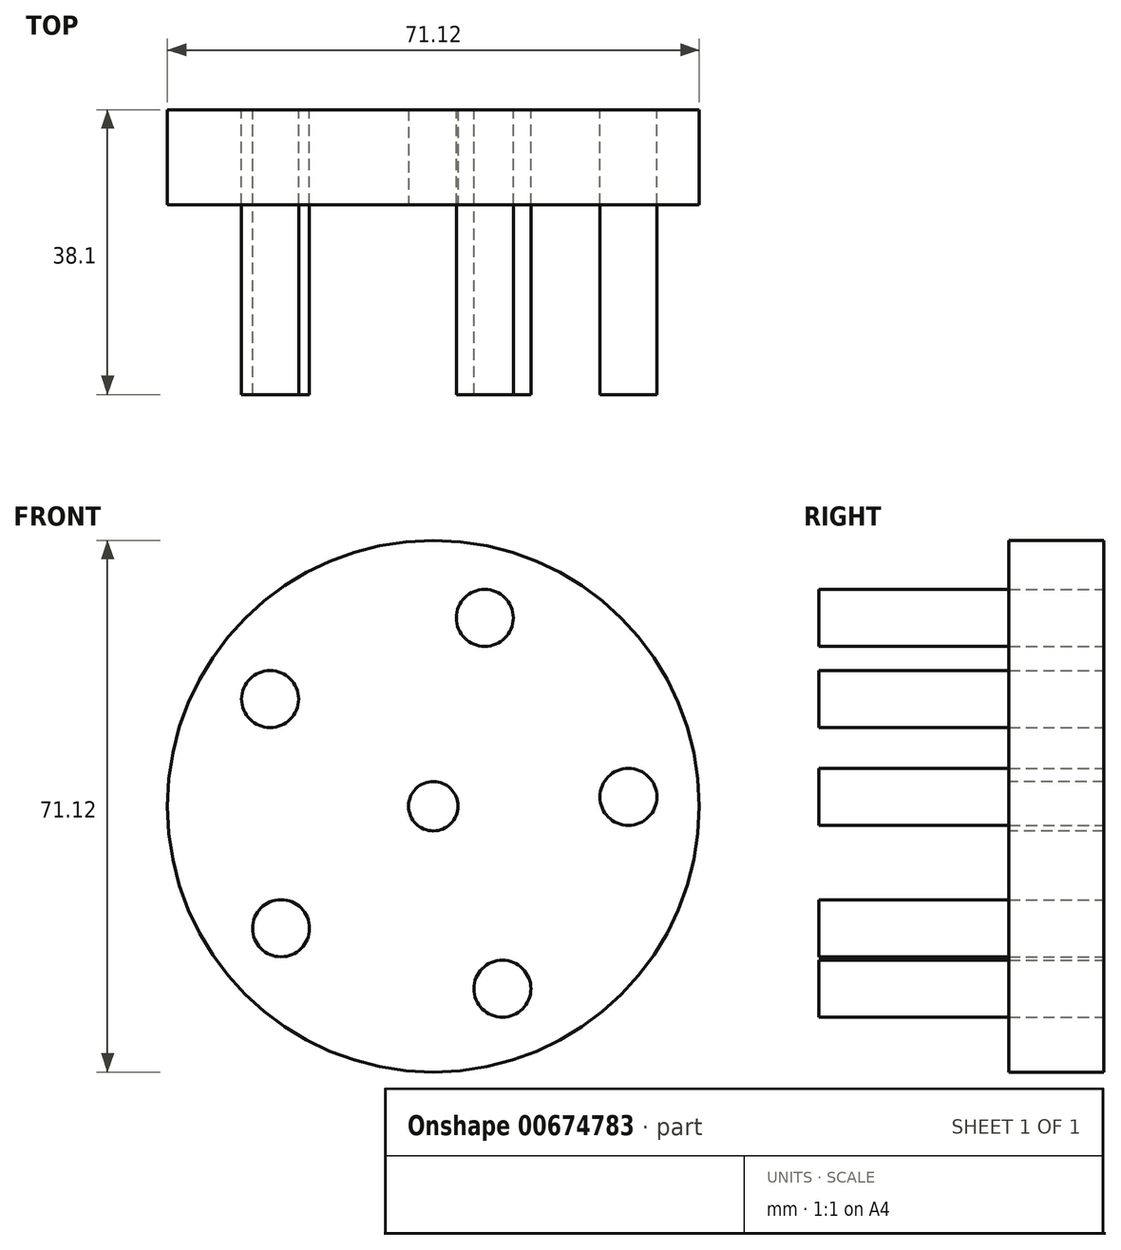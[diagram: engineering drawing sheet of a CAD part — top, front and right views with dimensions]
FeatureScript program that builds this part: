
annotation { "Feature Type Name" : "Feature", "Feature Type Description" : "" }
export const myFeature = defineFeature(function(context is Context, id is Id, definition is map)
    precondition{}
    {
        {
            var Q0;
            Q0=qCreatedBy(makeId("Front.planeOp"),FACE);
            var sketch = newSketch(context, id + "F0", { "sketchPlane" : qUnion([Q0])});
            skCircle(sketch, "E0", {"center": v(0, 0) * mm, "radius": 35.56 * mm});
            skLineSegment(sketch, "E1", {"start": v(11.25, 33.73) * mm, "end": v(8.5, 28.64) * mm});
            skCircle(sketch, "E2", {"center": v(6.88, 25.18) * mm, "radius": 3.81 * mm});
            skCircle(sketch, "E3.1.0", {"center": v(-21.83, 14.32) * mm, "radius": 3.81 * mm});
            skCircle(sketch, "E3.2.0", {"center": v(-20.37, -16.33) * mm, "radius": 3.81 * mm});
            skCircle(sketch, "E3.3.0", {"center": v(9.24, -24.42) * mm, "radius": 3.81 * mm});
            skCircle(sketch, "E3.4.0", {"center": v(26.08, 1.24) * mm, "radius": 3.81 * mm});
            skSolve(sketch);
        }
        {
            var Q0;
            Q0=makeQuery(id+"F0.imprint","IMPRINT",FACE,{"disambiguationData":[TD([[makeQuery(id+"F0.imprint","IMPRINT",EDGE,{"derivedFrom":sQuery(id+"F0.wireOp",EDGE,"E3.1.0")}),1.0]])]});
            var Q1;
            Q1=makeQuery(id+"F0.imprint","IMPRINT",FACE,{"disambiguationData":[TD([[makeQuery(id+"F0.imprint","IMPRINT",EDGE,{"derivedFrom":sQuery(id+"F0.wireOp",EDGE,"E2")}),1.0]])]});
            var Q2;
            Q2=makeQuery(id+"F0.imprint","IMPRINT",FACE,{"disambiguationData":[TD([[makeQuery(id+"F0.imprint","IMPRINT",EDGE,{"derivedFrom":sQuery(id+"F0.wireOp",EDGE,"E3.4.0")}),1.0]])]});
            var Q3;
            Q3=makeQuery(id+"F0.imprint","IMPRINT",FACE,{"disambiguationData":[TD([[makeQuery(id+"F0.imprint","IMPRINT",EDGE,{"derivedFrom":sQuery(id+"F0.wireOp",EDGE,"E3.3.0")}),1.0]])]});
            var Q4;
            Q4=makeQuery(id+"F0.imprint","IMPRINT",FACE,{"disambiguationData":[TD([[makeQuery(id+"F0.imprint","IMPRINT",EDGE,{"derivedFrom":sQuery(id+"F0.wireOp",EDGE,"E3.2.0")}),1.0]])]});
            extrude(context, id + "F1", {"entities" : qUnion([Q0, Q1, Q2, Q3, Q4]), "depth" : 38.1 * mm, "offsetDistance" : 25.4 * mm});
        }
        {
            var Q0;
            Q0 = qSketchRegion(id + "F0", true);
            extrude(context, id + "F2", {"entities" : qUnion([Q0]), "depth" : 12.7 * mm, "offsetDistance" : 25.4 * mm});
        }
        {
            var Q0;
            Q0=makeQuery(id+"F2.opExtrude","CAP_FACE",FACE,{"disambiguationData":[OSD([sQuery(id+"F0.wireOp",EDGE,"E0"),sQuery(id+"F0.wireOp",EDGE,"E2"),sQuery(id+"F0.wireOp",EDGE,"E3.1.0"),sQuery(id+"F0.wireOp",EDGE,"E3.2.0"),sQuery(id+"F0.wireOp",EDGE,"E3.3.0"),sQuery(id+"F0.wireOp",EDGE,"E3.4.0")])],"isStart":false});
            var sketch = newSketch(context, id + "F3", { "sketchPlane" : qUnion([Q0])});
            skCircle(sketch, "E4", {"center": v(0, 0) * mm, "radius": 3.3 * mm});
            skSolve(sketch);
        }
        {
            var Q0;
            Q0=makeQuery(id+"F3.imprint","IMPRINT",FACE,{"disambiguationData":[TD([[makeQuery(id+"F3.imprint","IMPRINT",EDGE,{"derivedFrom":sQuery(id+"F3.wireOp",EDGE,"E4")}),1.0]])]});
            extrude(context, id + "F4", {"entities" : qUnion([Q0]), "operationType" : NewBodyOperationType.REMOVE, "oppositeDirection" : true, "depth" : 25.4 * mm, "offsetDistance" : 25.4 * mm});
        }
    });
